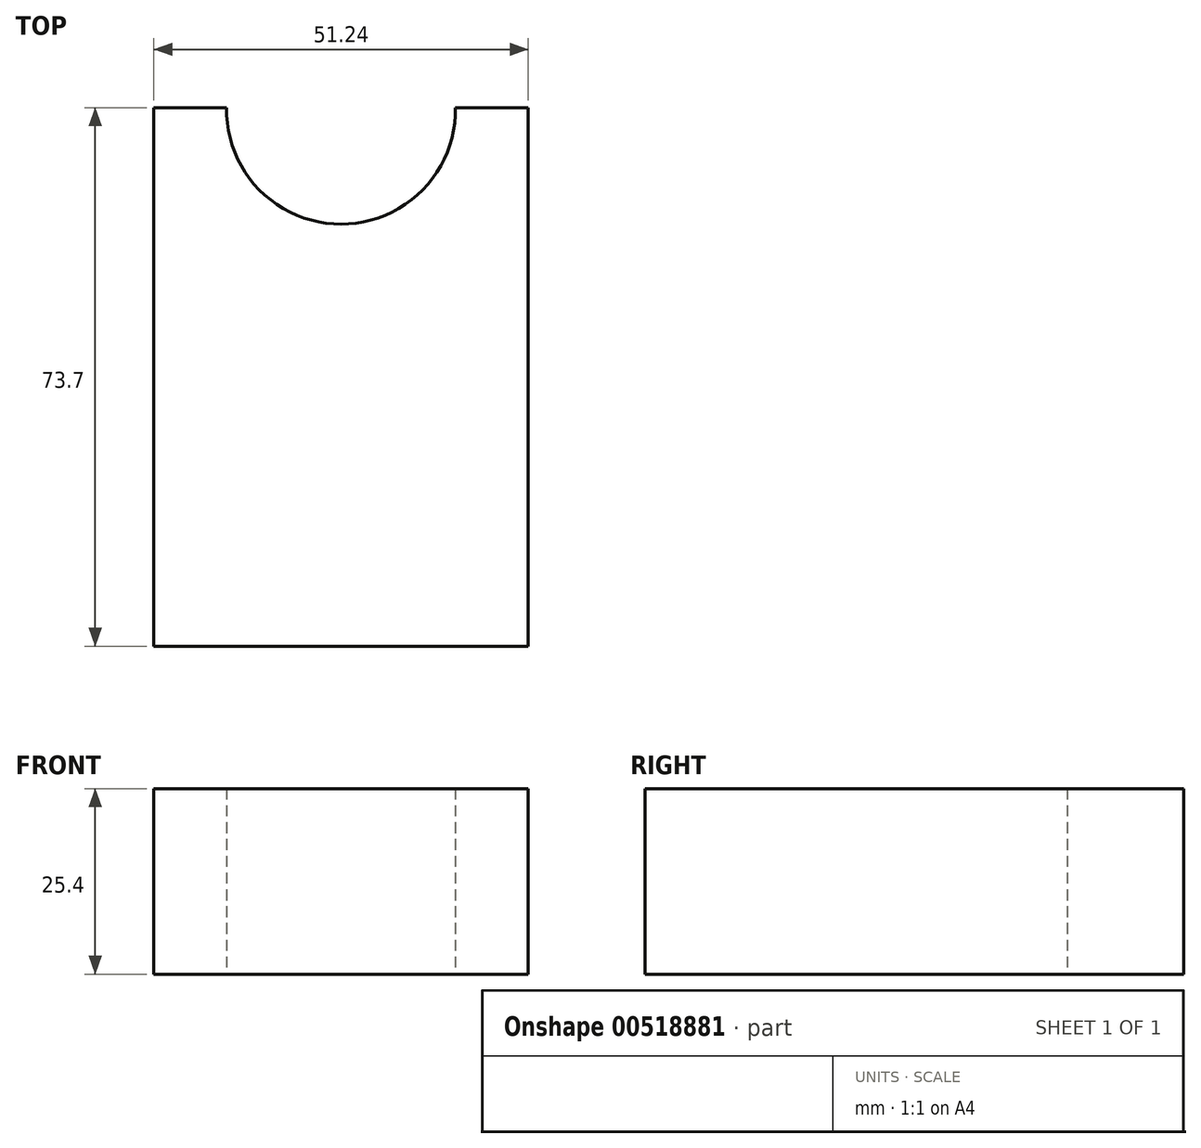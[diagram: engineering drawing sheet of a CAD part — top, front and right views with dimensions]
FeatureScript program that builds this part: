
annotation { "Feature Type Name" : "Feature", "Feature Type Description" : "" }
export const myFeature = defineFeature(function(context is Context, id is Id, definition is map)
    precondition{}
    {
        {
            var Q0;
            Q0=qCreatedBy(makeId("Top.planeOp"),FACE);
            var sketch = newSketch(context, id + "F0", { "sketchPlane" : qUnion([Q0])});
            skLineSegment(sketch, "E0.bottom", {"start": v(25.62, 36.85) * mm, "end": v(-25.62, 36.85) * mm});
            skLineSegment(sketch, "E0.top", {"start": v(25.62, -36.85) * mm, "end": v(-25.62, -36.85) * mm});
            skLineSegment(sketch, "E0.left", {"start": v(25.62, 36.85) * mm, "end": v(25.62, -36.85) * mm});
            skLineSegment(sketch, "E0.right", {"start": v(-25.62, 36.85) * mm, "end": v(-25.62, -36.85) * mm});
            skPoint(sketch, "E0.middle", {"position": v(0, 0) * mm});
            skSolve(sketch);
        }
        {
            var Q0;
            Q0=makeQuery(id+"F0.imprint","IMPRINT",FACE,{"disambiguationData":[TD([[makeQuery(id+"F0.imprint","IMPRINT",EDGE,{"derivedFrom":sQuery(id+"F0.wireOp",EDGE,"E0.bottom")}),1.0]])]});
            var sketch = newSketch(context, id + "F1", { "sketchPlane" : qUnion([Q0])});
            skArc(sketch, "E1", {"start": v(-25.53, 36.31) * mm, "mid": v(0.13, 62.12) * mm, "end": v(25.52, 36.04) * mm});
            skCircle(sketch, "E2", {"center": v(0, 36.59) * mm, "radius": 15.67 * mm});
            skSolve(sketch);
        }
        {
            var Q0;
            Q0=makeQuery(id+"F1.imprint","IMPRINT",FACE,{"disambiguationData":[TD([[makeQuery(id+"F1.imprint","IMPRINT",EDGE,{"derivedFrom":makeQuery(id+"F0.imprint","IMPRINT",EDGE,{"derivedFrom":sQuery(id+"F0.wireOp",EDGE,"E0.top")})}),-1.0]])]});
            var Q1;
            {var subQ0=sQuery(id+"F1.wireOp",EDGE,"E1");var subQ1=makeQuery(id+"F0.imprint","IMPRINT",EDGE,{"derivedFrom":sQuery(id+"F0.wireOp",EDGE,"E0.bottom")});var subQ2=makeQuery(id+"F1.imprint","INTERSECT",VERTEX,{"disambiguationData":[OD(0.0)],"derivedFrom":[subQ1,subQ0]});Q1=makeQuery(id+"F1.imprint","IMPRINT",FACE,{"disambiguationData":[TD([[makeQuery(id+"F1.imprint","IMPRINT",EDGE,{"disambiguationData":[TD([[subQ2,1.0]])],"derivedFrom":subQ0}),-1.0]])]});}
            extrude(context, id + "F2", {"entities" : qUnion([Q0, Q1]), "depth" : 25.4 * mm});
        }
    });
